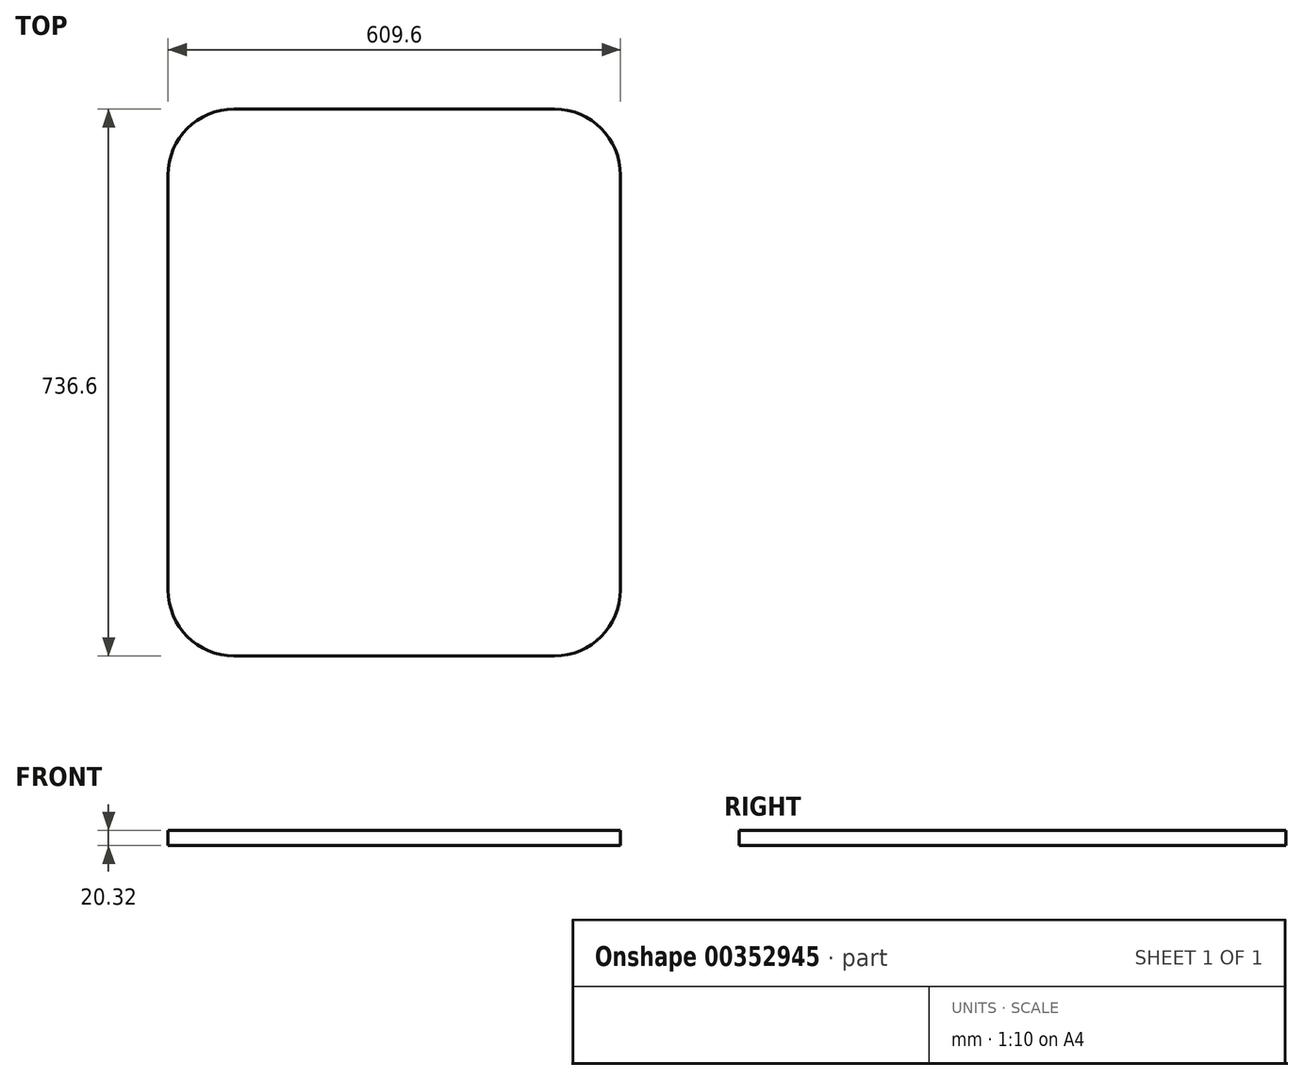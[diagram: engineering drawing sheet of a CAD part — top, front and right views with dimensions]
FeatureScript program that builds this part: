
annotation { "Feature Type Name" : "Feature", "Feature Type Description" : "" }
export const myFeature = defineFeature(function(context is Context, id is Id, definition is map)
    precondition{}
    {
        {
            var Q0;
            Q0=qCreatedBy(makeId("Top.planeOp"),FACE);
            var sketch = newSketch(context, id + "F0", { "sketchPlane" : qUnion([Q0])});
            skLineSegment(sketch, "E0.bottom", {"start": v(-215.9, -381) * mm, "end": v(-190.5, -381) * mm});
            skLineSegment(sketch, "E0.top", {"start": v(-215.9, 381) * mm, "end": v(215.9, 381) * mm, "construction": true});
            skLineSegment(sketch, "E0.left", {"start": v(-317.5, -279.4) * mm, "end": v(-317.5, 279.4) * mm, "construction": true});
            skLineSegment(sketch, "E0.right", {"start": v(317.5, -279.4) * mm, "end": v(317.5, 279.4) * mm, "construction": true});
            skPoint(sketch, "E0.middle", {"position": v(0, 0) * mm});
            skPoint(sketch, "E1.visualSharp", {"position": v(-317.5, 381) * mm});
            skArc(sketch, "E1.filletArc", {"start": v(-215.9, 381) * mm, "mid": v(-287.74, 351.24) * mm, "end": v(-317.5, 279.4) * mm, "construction": true});
            skPoint(sketch, "E2.visualSharp", {"position": v(317.5, 381) * mm});
            skArc(sketch, "E2.filletArc", {"start": v(317.5, 279.4) * mm, "mid": v(287.74, 351.24) * mm, "end": v(215.9, 381) * mm, "construction": true});
            skPoint(sketch, "E3.visualSharp", {"position": v(-317.5, -381) * mm});
            skArc(sketch, "E3.filletArc", {"start": v(-317.5, -279.4) * mm, "mid": v(-287.74, -351.24) * mm, "end": v(-215.9, -381) * mm, "construction": true});
            skPoint(sketch, "E4.visualSharp", {"position": v(317.5, -381) * mm});
            skArc(sketch, "E4.filletArc", {"start": v(215.9, -381) * mm, "mid": v(287.74, -351.24) * mm, "end": v(317.5, -279.4) * mm, "construction": true});
            skArc(sketch, "E5.0", {"start": v(215.9, -368.3) * mm, "mid": v(278.76, -342.26) * mm, "end": v(304.8, -279.4) * mm});
            skLineSegment(sketch, "E5.1", {"start": v(-215.9, -368.3) * mm, "end": v(-190.5, -368.3) * mm});
            skLineSegment(sketch, "E5.2", {"start": v(304.8, -279.4) * mm, "end": v(304.8, 279.4) * mm});
            skArc(sketch, "E5.3", {"start": v(-304.8, -279.4) * mm, "mid": v(-278.76, -342.26) * mm, "end": v(-215.9, -368.3) * mm});
            skArc(sketch, "E5.4", {"start": v(304.8, 279.4) * mm, "mid": v(278.76, 342.26) * mm, "end": v(215.9, 368.3) * mm});
            skLineSegment(sketch, "E5.5", {"start": v(-215.9, 368.3) * mm, "end": v(215.9, 368.3) * mm});
            skArc(sketch, "E5.6", {"start": v(-215.9, 368.3) * mm, "mid": v(-278.76, 342.26) * mm, "end": v(-304.8, 279.4) * mm});
            skLineSegment(sketch, "E5.7", {"start": v(-304.8, -279.4) * mm, "end": v(-304.8, 279.4) * mm});
            skLineSegment(sketch, "E6", {"start": v(0, 698.7) * mm, "end": v(0, -611.94) * mm, "construction": true});
            skPoint(sketch, "E6.endSnap0", {"position": v(0, -381) * mm});
            skLineSegment(sketch, "E7.trimOffspring", {"start": v(190.5, -381) * mm, "end": v(215.9, -381) * mm});
            skLineSegment(sketch, "E8.trimOffspring", {"start": v(190.5, -368.3) * mm, "end": v(215.9, -368.3) * mm});
            skLineSegment(sketch, "E9", {"start": v(-190.5, -368.3) * mm, "end": v(190.5, -368.3) * mm});
            skSolve(sketch);
        }
        {
            var Q0;
            Q0 = qSketchRegion(id + "F0", true);
            extrude(context, id + "F1", {"entities" : qUnion([Q0]), "depth" : 20.32 * mm});
        }
    });
